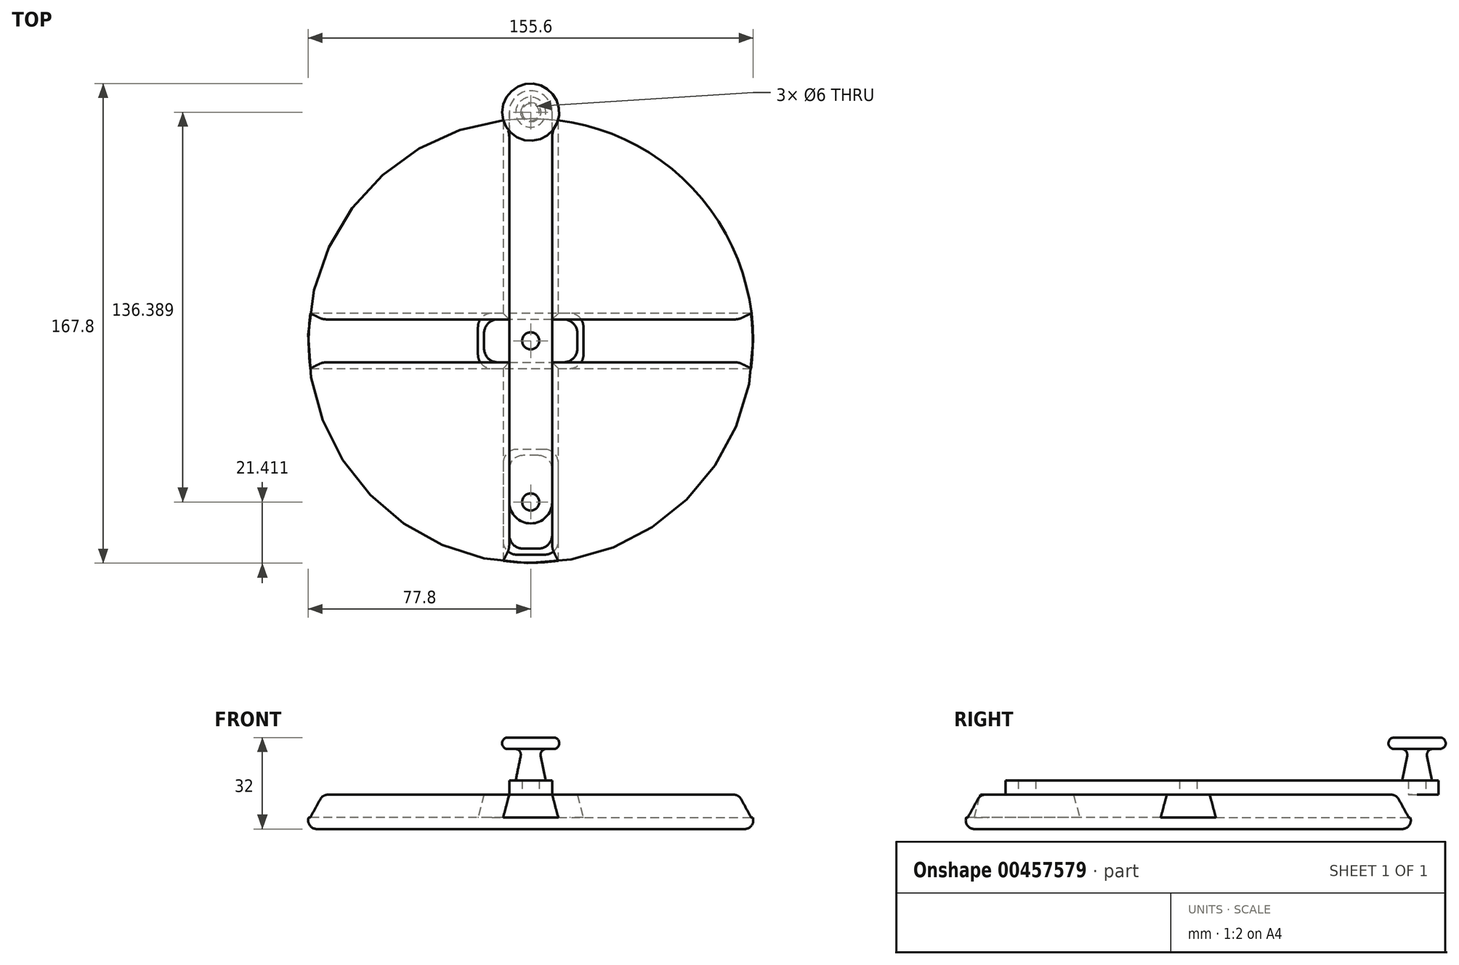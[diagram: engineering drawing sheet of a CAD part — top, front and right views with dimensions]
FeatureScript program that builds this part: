
annotation { "Feature Type Name" : "Feature", "Feature Type Description" : "" }
export const myFeature = defineFeature(function(context is Context, id is Id, definition is map)
    precondition{}
    {
        {
            var Q0;
            Q0=qCreatedBy(makeId("Top.planeOp"),FACE);
            var sketch = newSketch(context, id + "F0", { "sketchPlane" : qUnion([Q0])});
            skCircle(sketch, "E0", {"center": v(0, 0) * mm, "radius": 80 * mm});
            skSolve(sketch);
        }
        {
            var Q0;
            Q0 = qSketchRegion(id + "F0", true);
            extrude(context, id + "F1", {"entities" : qUnion([Q0]), "depth" : 12 * mm, "hasDraft" : true, "draftAngle" : 30 * degree, "draftPullDirection" : true});
        }
        {
            var Q0;
            Q0=makeQuery(id+"F1.opExtrude","CAP_FACE",FACE,{"disambiguationData":[OSD([sQuery(id+"F0.wireOp",EDGE,"E0")])],"isStart":false});
            var sketch = newSketch(context, id + "F2", { "sketchPlane" : qUnion([Q0])});
            skLineSegment(sketch, "E1.bottom", {"start": v(7.5, -79.65) * mm, "end": v(-7.5, -79.65) * mm});
            skLineSegment(sketch, "E1.top", {"start": v(7.5, 79.65) * mm, "end": v(-7.5, 79.65) * mm});
            skLineSegment(sketch, "E1.left", {"start": v(7.5, -79.65) * mm, "end": v(7.5, 79.65) * mm});
            skLineSegment(sketch, "E1.right", {"start": v(-7.5, -79.65) * mm, "end": v(-7.5, 79.65) * mm});
            skPoint(sketch, "E1.middle", {"position": v(0, 0) * mm});
            skLineSegment(sketch, "E2.bottom", {"start": v(79.65, -7.5) * mm, "end": v(-79.65, -7.5) * mm});
            skLineSegment(sketch, "E2.top", {"start": v(79.65, 7.5) * mm, "end": v(-79.65, 7.5) * mm});
            skLineSegment(sketch, "E2.left", {"start": v(79.65, -7.5) * mm, "end": v(79.65, 7.5) * mm});
            skLineSegment(sketch, "E2.right", {"start": v(-79.65, -7.5) * mm, "end": v(-79.65, 7.5) * mm});
            skCircle(sketch, "E3.0", {"center": v(0, 0) * mm, "radius": 80 * mm, "construction": true});
            skSolve(sketch);
        }
        {
            var Q0;
            Q0 = qSketchRegion(id + "F2", true);
            extrude(context, id + "F3", {"entities" : qUnion([Q0]), "operationType" : NewBodyOperationType.REMOVE, "oppositeDirection" : true, "depth" : 8 * mm, "hasDraft" : true, "draftAngle" : 15 * degree});
        }
        {
            var Q0;
            {var subQ0=sQuery(id+"F0.wireOp",EDGE,"E0");var subQ1=sQuery(id+"F2.wireOp",EDGE,"E2.bottom");var subQ4=sQuery(id+"F2.wireOp",EDGE,"E1.right");var subQ5=makeQuery(id+"F2.imprint","INTERSECT",VERTEX,{"derivedFrom":[subQ4,subQ1]});Q0=makeQuery(id+"F3.boolean.opBoolean","SPLIT",FACE,{"disambiguationData":[TD([makeQuery(id+"F3.opExtrude","SWEPT_FACE",FACE,{"disambiguationData":[OSD([subQ4]),TDD([makeQuery(id+"F2.imprint","IMPRINT",EDGE,{"disambiguationData":[TD([[makeQuery(id+"F2.imprint","INTERSECT",VERTEX,{"derivedFrom":[sQuery(id+"F2.wireOp",EDGE,"E1.bottom"),subQ4]}),-1.0]])],"derivedFrom":subQ4}),makeQuery(id+"F2.imprint","IMPRINT",EDGE,{"disambiguationData":[TD([[subQ5,1.0]])],"derivedFrom":subQ4})])]})])],"derivedFrom":makeQuery(id+"F1.opExtrude","CAP_FACE",FACE,{"disambiguationData":[OSD([subQ0])],"isStart":false})});}
            var sketch = newSketch(context, id + "F4", { "sketchPlane" : qUnion([Q0])});
            skLineSegment(sketch, "E4.bottom", {"start": v(-7.5, -72.69) * mm, "end": v(7.5, -72.69) * mm});
            skLineSegment(sketch, "E4.top", {"start": v(-7.5, -40.1) * mm, "end": v(7.5, -40.1) * mm});
            skLineSegment(sketch, "E4.left", {"start": v(-7.5, -72.69) * mm, "end": v(-7.5, -40.1) * mm});
            skLineSegment(sketch, "E4.right", {"start": v(7.5, -72.69) * mm, "end": v(7.5, -40.1) * mm});
            skPoint(sketch, "E4.middle", {"position": v(0, -56.39) * mm});
            skLineSegment(sketch, "E5.bottom", {"start": v(-16.3, -7.5) * mm, "end": v(16.3, -7.5) * mm});
            skLineSegment(sketch, "E5.top", {"start": v(-16.3, 7.5) * mm, "end": v(16.3, 7.5) * mm});
            skLineSegment(sketch, "E5.left", {"start": v(-16.3, -7.5) * mm, "end": v(-16.3, 7.5) * mm});
            skLineSegment(sketch, "E5.right", {"start": v(16.3, -7.5) * mm, "end": v(16.3, 7.5) * mm});
            skPoint(sketch, "E5.middle", {"position": v(0, 0) * mm});
            skSolve(sketch);
        }
        {
            var Q0;
            Q0 = qSketchRegion(id + "F4", true);
            extrude(context, id + "F5", {"entities" : qUnion([Q0]), "oppositeDirection" : true, "depth" : 8 * mm, "hasDraft" : true, "draftAngle" : 15 * degree});
        }
        {
            var Q0;
            {var subQ11=sQuery(id+"F4.wireOp",EDGE,"E4.left");Q0=makeQuery(id+"F4.imprint","IMPRINT",FACE,{"disambiguationData":[TD([[makeQuery(id+"F4.imprint","IMPRINT",EDGE,{"derivedFrom":subQ11}),1.0]])]});}
            var sketch = newSketch(context, id + "F6", { "sketchPlane" : qUnion([Q0])});
            skPoint(sketch, "E6.0", {"position": v(0, -56.39) * mm});
            skPoint(sketch, "E7.0", {"position": v(0, 0) * mm});
            skCircle(sketch, "E8", {"center": v(0, 0) * mm, "radius": 3 * mm});
            skCircle(sketch, "E9", {"center": v(0, -56.39) * mm, "radius": 3 * mm});
            skSolve(sketch);
        }
        {
            var Q0;
            Q0 = qSketchRegion(id + "F6", true);
            extrude(context, id + "F7", {"entities" : qUnion([Q0]), "operationType" : NewBodyOperationType.ADD, "depth" : 5 * mm});
        }
        {
            var Q0;
            Q0 = qSketchRegion(id + "F4", true);
            var sketch = newSketch(context, id + "F8", { "sketchPlane" : qUnion([Q0])});
            skPoint(sketch, "E10.0", {"position": v(0, -56.39) * mm});
            skLineSegment(sketch, "E11", {"start": v(0, -56.39) * mm, "end": v(0, 80) * mm, "construction": true});
            skArc(sketch, "E12.0.startCap", {"start": v(7.5, -56.39) * mm, "mid": v(0, -63.89) * mm, "end": v(-7.5, -56.39) * mm});
            skArc(sketch, "E12.0.endCap", {"start": v(-7.5, 80) * mm, "mid": v(0, 87.5) * mm, "end": v(7.5, 80) * mm});
            skLineSegment(sketch, "E12.0.left", {"start": v(-7.5, -56.39) * mm, "end": v(-7.5, 80) * mm});
            skLineSegment(sketch, "E12.0.right", {"start": v(7.5, -56.39) * mm, "end": v(7.5, 80) * mm});
            skCircle(sketch, "E13.0", {"center": v(0, -56.39) * mm, "radius": 3 * mm});
            skCircle(sketch, "E13.1.0", {"center": v(0, 0) * mm, "radius": 3 * mm});
            skCircle(sketch, "E14", {"center": v(0, 80) * mm, "radius": 3 * mm});
            skSolve(sketch);
        }
        {
            var Q0;
            Q0 = qSketchRegion(id + "F8", true);
            var Q1;
            Q1=makeQuery(id+"F7.opExtrude","CAP_FACE",FACE,{"disambiguationData":[OSD([sQuery(id+"F6.wireOp",EDGE,"E8")])],"isStart":false});
            extrude(context, id + "F9", {"entities" : qUnion([Q0]), "endBound" : BoundingType.UP_TO_SURFACE, "endBoundEntityFace" : qUnion([Q1]), "depth" : 25 * mm});
        }
        {
            var Q0;
            Q0=qCreatedBy(makeId("Front.planeOp"),FACE);
            var Q1;
            Q1=sQuery(id+"F8.wireOp",VERTEX,"E12.0.endCap.center");
            cPlane(context, id + "F10", {"entities" : qUnion([Q0, Q1]), "cplaneType" : CPlaneType.PLANE_POINT, "offset" : 25 * mm, "width" : 150 * mm, "height" : 150 * mm});
        }
        {
            var Q0;
            Q0=qCreatedBy(id+"F10.planeOp",FACE);
            var sketch = newSketch(context, id + "F11", { "sketchPlane" : qUnion([Q0])});
            skLineSegment(sketch, "E15.0", {"start": v(-3, 12) * mm, "end": v(3, 12) * mm});
            skLineSegment(sketch, "E16", {"start": v(0, 12) * mm, "end": v(0, 32) * mm});
            skLineSegment(sketch, "E17", {"start": v(0, 32) * mm, "end": v(-8, 32) * mm});
            skLineSegment(sketch, "E18", {"start": v(-10, 30) * mm, "end": v(-10, 30) * mm});
            skLineSegment(sketch, "E19", {"start": v(-8, 28) * mm, "end": v(-5.45, 28) * mm});
            skLineSegment(sketch, "E20", {"start": v(-3.5, 25.6) * mm, "end": v(-5.25, 17) * mm});
            skLineSegment(sketch, "E21", {"start": v(-5.25, 17) * mm, "end": v(-3, 17) * mm});
            skLineSegment(sketch, "E22", {"start": v(3, 17) * mm, "end": v(3, 12) * mm, "construction": true});
            skLineSegment(sketch, "E23", {"start": v(-3, 28) * mm, "end": v(-3, 17) * mm, "construction": true});
            skLineSegment(sketch, "E24.0", {"start": v(-7.5, 17) * mm, "end": v(-7.5, 12) * mm, "construction": true});
            skLineSegment(sketch, "E25", {"start": v(-3, 17) * mm, "end": v(-7.5, 17) * mm});
            skPoint(sketch, "E26.visualSharp", {"position": v(-10, 32) * mm});
            skArc(sketch, "E26.filletArc", {"start": v(-8, 32) * mm, "mid": v(-9.41, 31.41) * mm, "end": v(-10, 30) * mm});
            skPoint(sketch, "E27.visualSharp", {"position": v(-10, 28) * mm});
            skArc(sketch, "E27.filletArc", {"start": v(-10, 30) * mm, "mid": v(-9.41, 28.59) * mm, "end": v(-8, 28) * mm});
            skPoint(sketch, "E28.visualSharp", {"position": v(-3, 28) * mm});
            skArc(sketch, "E28.filletArc", {"start": v(-3.5, 25.6) * mm, "mid": v(-3.9, 27.26) * mm, "end": v(-5.45, 28) * mm});
            skLineSegment(sketch, "E29", {"start": v(-3, 17) * mm, "end": v(-3, 12) * mm});
            skSolve(sketch);
        }
        {
            var Q0;
            Q0 = qSketchRegion(id + "F11", true);
            var Q1;
            Q1=sQuery(id+"F11.wireOp",EDGE,"E16");
            revolve(context, id + "F12", {"entities" : qUnion([Q0]), "axis" : qUnion([Q1]), "revolveType" : RevolveType.FULL});
        }
        {
            var Q0;
            Q0=makeQuery(id+"F5.opExtrude","SWEPT_EDGE",EDGE,{"disambiguationData":[OSD([sQuery(id+"F0.wireOp",EDGE,"E0"),sQuery(id+"F4.wireOp",EDGE,"E4.bottom"),sQuery(id+"F4.wireOp",EDGE,"E4.left")])]});
            var Q1;
            Q1=makeQuery(id+"F5.opExtrude","SWEPT_EDGE",EDGE,{"disambiguationData":[OSD([sQuery(id+"F4.wireOp",EDGE,"E4.bottom"),sQuery(id+"F4.wireOp",EDGE,"E4.right")])]});
            var Q2;
            Q2=makeQuery(id+"F5.opExtrude","SWEPT_EDGE",EDGE,{"disambiguationData":[OSD([sQuery(id+"F4.wireOp",EDGE,"E4.top"),sQuery(id+"F4.wireOp",EDGE,"E4.right")])]});
            var Q3;
            Q3=makeQuery(id+"F5.opExtrude","SWEPT_EDGE",EDGE,{"disambiguationData":[OSD([sQuery(id+"F2.wireOp",EDGE,"E2.bottom"),sQuery(id+"F4.wireOp",EDGE,"E5.bottom"),sQuery(id+"F4.wireOp",EDGE,"E5.left")])]});
            var Q4;
            Q4=makeQuery(id+"F5.opExtrude","SWEPT_EDGE",EDGE,{"disambiguationData":[OSD([sQuery(id+"F4.wireOp",EDGE,"E5.bottom"),sQuery(id+"F4.wireOp",EDGE,"E5.right")])]});
            var Q5;
            Q5=makeQuery(id+"F5.opExtrude","SWEPT_EDGE",EDGE,{"disambiguationData":[OSD([sQuery(id+"F4.wireOp",EDGE,"E5.top"),sQuery(id+"F4.wireOp",EDGE,"E5.right")])]});
            var Q6;
            Q6=makeQuery(id+"F5.opExtrude","SWEPT_EDGE",EDGE,{"disambiguationData":[OSD([sQuery(id+"F2.wireOp",EDGE,"E1.right"),sQuery(id+"F4.wireOp",EDGE,"E4.top"),sQuery(id+"F4.wireOp",EDGE,"E4.left")])]});
            var Q7;
            Q7=makeQuery(id+"F5.opExtrude","SWEPT_EDGE",EDGE,{"disambiguationData":[OSD([sQuery(id+"F4.wireOp",EDGE,"E5.top"),sQuery(id+"F4.wireOp",EDGE,"E5.left")])]});
            fillet(context, id + "F13", {"entities" : qUnion([Q0, Q1, Q2, Q3, Q4, Q5, Q6, Q7]), "radius" : 5 * mm, "tangentPropagation" : true, "allowEdgeOverflow" : false});
        }
        {
            var Q0;
            {var subQ0=sQuery(id+"F8.wireOp",EDGE,"E12.0.right");var subQ1=makeQuery(id+"F8.imprint","INTERSECT",VERTEX,{"derivedFrom":[makeQuery(id+"F4.imprint","IMPRINT",EDGE,{"derivedFrom":sQuery(id+"F4.wireOp",EDGE,"E5.top")}),subQ0]});Q0=makeQuery(id+"F9.opExtrude","TWEAK_EDGE",EDGE,{"derivedFrom":[makeQuery(id+"F7.opExtrude","CAP_FACE",FACE,{"disambiguationData":[OSD([sQuery(id+"F6.wireOp",EDGE,"E8")])],"isStart":false}),makeQuery(id+"F8.imprint","IMPRINT",EDGE,{"disambiguationData":[TD([[makeQuery(id+"F8.imprint","INTERSECT",VERTEX,{"derivedFrom":[sQuery(id+"F8.wireOp",EDGE,"E12.0.startCap"),subQ0]}),-1.0]])],"derivedFrom":subQ0}),makeQuery(id+"F8.imprint","IMPRINT",EDGE,{"disambiguationData":[TD([[subQ1,1.0]])],"derivedFrom":subQ0}),makeQuery(id+"F8.imprint","IMPRINT",EDGE,{"disambiguationData":[TD([[makeQuery(id+"F8.imprint","INTERSECT",VERTEX,{"derivedFrom":[sQuery(id+"F8.wireOp",EDGE,"E12.0.endCap"),subQ0]}),1.0]])],"derivedFrom":subQ0})]});}
            var Q1;
            Q1=makeQuery(id+"F1.opExtrude","CAP_FACE",FACE,{"disambiguationData":[OSD([sQuery(id+"F0.wireOp",EDGE,"E0")])],"isStart":true});
            var Q2;
            {var subQ0=sQuery(id+"F0.wireOp",EDGE,"E0");var subQ1=sQuery(id+"F2.wireOp",EDGE,"E2.bottom");var subQ2=makeQuery(id+"F1.opExtrude","CAP_EDGE",EDGE,{"disambiguationData":[OSD([subQ0])],"isStart":false});var subQ4=sQuery(id+"F2.wireOp",EDGE,"E1.right");var subQ5=makeQuery(id+"F2.imprint","INTERSECT",VERTEX,{"derivedFrom":[subQ4,subQ1]});Q2=makeQuery(id+"F3.boolean.opBoolean","SPLIT",EDGE,{"disambiguationData":[TD([makeQuery(id+"F3.opExtrude","SWEPT_FACE",FACE,{"disambiguationData":[OSD([subQ4]),TDD([makeQuery(id+"F2.imprint","IMPRINT",EDGE,{"disambiguationData":[TD([[makeQuery(id+"F2.imprint","INTERSECT",VERTEX,{"derivedFrom":[sQuery(id+"F2.wireOp",EDGE,"E1.bottom"),subQ4]}),-1.0]])],"derivedFrom":subQ4}),makeQuery(id+"F2.imprint","IMPRINT",EDGE,{"disambiguationData":[TD([[subQ5,1.0]])],"derivedFrom":subQ4})])]})])],"derivedFrom":subQ2});}
            var Q3;
            {var subQ0=sQuery(id+"F0.wireOp",EDGE,"E0");var subQ1=sQuery(id+"F2.wireOp",EDGE,"E2.top");var subQ2=makeQuery(id+"F1.opExtrude","CAP_EDGE",EDGE,{"disambiguationData":[OSD([subQ0])],"isStart":false});var subQ4=sQuery(id+"F2.wireOp",EDGE,"E1.right");var subQ5=makeQuery(id+"F2.imprint","INTERSECT",VERTEX,{"derivedFrom":[subQ4,subQ1]});Q3=makeQuery(id+"F3.boolean.opBoolean","SPLIT",EDGE,{"disambiguationData":[TD([makeQuery(id+"F3.opExtrude","SWEPT_FACE",FACE,{"disambiguationData":[OSD([subQ4]),TDD([makeQuery(id+"F2.imprint","IMPRINT",EDGE,{"disambiguationData":[TD([[subQ5,-1.0]])],"derivedFrom":subQ4}),makeQuery(id+"F2.imprint","IMPRINT",EDGE,{"disambiguationData":[TD([[makeQuery(id+"F2.imprint","INTERSECT",VERTEX,{"derivedFrom":[sQuery(id+"F2.wireOp",EDGE,"E1.top"),subQ4]}),1.0]])],"derivedFrom":subQ4})])]})])],"derivedFrom":subQ2});}
            var Q4;
            {var subQ0=sQuery(id+"F0.wireOp",EDGE,"E0");var subQ1=sQuery(id+"F2.wireOp",EDGE,"E1.left");var subQ2=makeQuery(id+"F1.opExtrude","CAP_EDGE",EDGE,{"disambiguationData":[OSD([subQ0])],"isStart":false});var subQ4=sQuery(id+"F2.wireOp",EDGE,"E2.top");var subQ5=makeQuery(id+"F2.imprint","INTERSECT",VERTEX,{"derivedFrom":[subQ1,subQ4]});Q4=makeQuery(id+"F3.boolean.opBoolean","SPLIT",EDGE,{"disambiguationData":[TD([makeQuery(id+"F3.opExtrude","SWEPT_FACE",FACE,{"disambiguationData":[OSD([subQ1]),TDD([makeQuery(id+"F2.imprint","IMPRINT",EDGE,{"disambiguationData":[TD([[subQ5,-1.0]])],"derivedFrom":subQ1}),makeQuery(id+"F2.imprint","IMPRINT",EDGE,{"disambiguationData":[TD([[makeQuery(id+"F2.imprint","INTERSECT",VERTEX,{"derivedFrom":[sQuery(id+"F2.wireOp",EDGE,"E1.top"),subQ1]}),1.0]])],"derivedFrom":subQ1})])]})])],"derivedFrom":subQ2});}
            var Q5;
            {var subQ0=sQuery(id+"F0.wireOp",EDGE,"E0");var subQ1=sQuery(id+"F2.wireOp",EDGE,"E2.bottom");var subQ2=sQuery(id+"F2.wireOp",EDGE,"E1.left");var subQ3=makeQuery(id+"F2.imprint","INTERSECT",VERTEX,{"derivedFrom":[subQ2,subQ1]});var subQ4=makeQuery(id+"F1.opExtrude","CAP_EDGE",EDGE,{"disambiguationData":[OSD([subQ0])],"isStart":false});Q5=makeQuery(id+"F3.boolean.opBoolean","SPLIT",EDGE,{"disambiguationData":[TD([makeQuery(id+"F3.opExtrude","SWEPT_FACE",FACE,{"disambiguationData":[OSD([subQ2]),TDD([makeQuery(id+"F2.imprint","IMPRINT",EDGE,{"disambiguationData":[TD([[makeQuery(id+"F2.imprint","INTERSECT",VERTEX,{"derivedFrom":[sQuery(id+"F2.wireOp",EDGE,"E1.bottom"),subQ2]}),-1.0]])],"derivedFrom":subQ2}),makeQuery(id+"F2.imprint","IMPRINT",EDGE,{"disambiguationData":[TD([[subQ3,1.0]])],"derivedFrom":subQ2})])]})])],"derivedFrom":subQ4});}
            fillet(context, id + "F14", {"entities" : qUnion([Q0, Q1, Q2, Q3, Q4, Q5]), "radius" : 3 * mm, "tangentPropagation" : true, "allowEdgeOverflow" : false});
        }
    });
